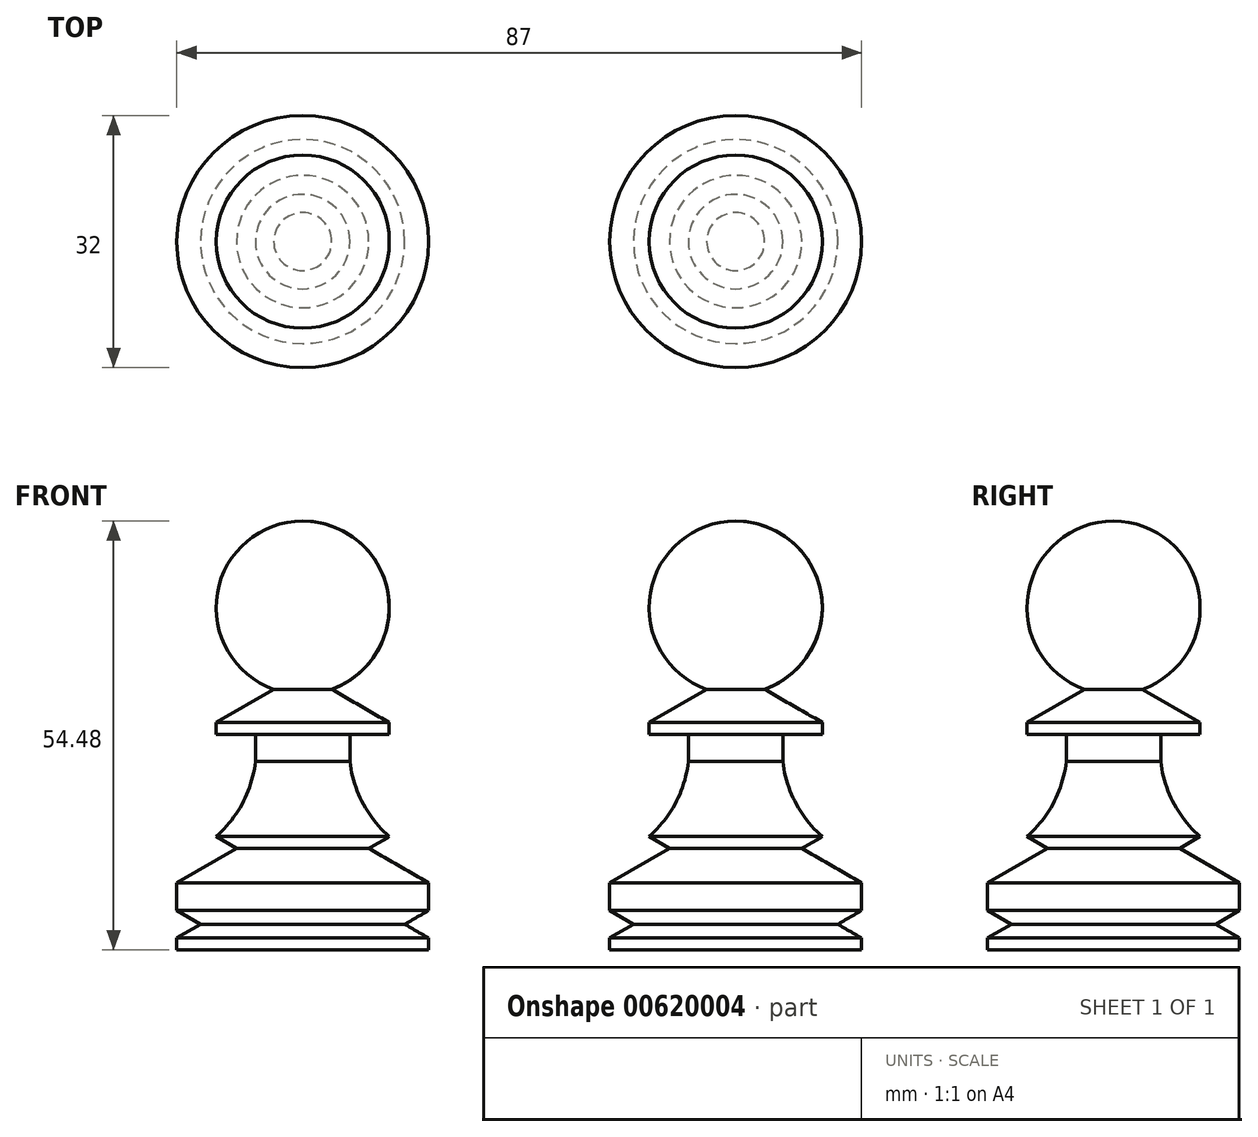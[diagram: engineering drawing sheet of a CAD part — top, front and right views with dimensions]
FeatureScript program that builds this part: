
annotation { "Feature Type Name" : "Feature", "Feature Type Description" : "" }
export const myFeature = defineFeature(function(context is Context, id is Id, definition is map)
    precondition{}
    {
        {
            var Q0;
            Q0=qCreatedBy(makeId("Front.planeOp"),FACE);
            var sketch = newSketch(context, id + "F0", { "sketchPlane" : qUnion([Q0])});
            skLineSegment(sketch, "E0", {"start": v(0, 0) * mm, "end": v(16, 0) * mm});
            skLineSegment(sketch, "E1", {"start": v(16, 0) * mm, "end": v(16, 1.5) * mm});
            skLineSegment(sketch, "E2", {"start": v(16, 1.5) * mm, "end": v(12.97, 3.25) * mm});
            skLineSegment(sketch, "E3", {"start": v(0, 0) * mm, "end": v(0, 5) * mm});
            skLineSegment(sketch, "E4", {"start": v(0, 5) * mm, "end": v(16, 5) * mm});
            skLineSegment(sketch, "E5", {"start": v(16, 5) * mm, "end": v(12.97, 3.25) * mm});
            skPoint(sketch, "E6.orphan", {"position": v(9.94, 1.5) * mm});
            skLineSegment(sketch, "E7", {"start": v(16, 5) * mm, "end": v(16, 8.5) * mm});
            skLineSegment(sketch, "E8", {"start": v(16, 8.5) * mm, "end": v(0, 8.5) * mm});
            skLineSegment(sketch, "E9", {"start": v(16, 8.5) * mm, "end": v(8.4, 12.89) * mm});
            skLineSegment(sketch, "E10", {"start": v(11, 12.89) * mm, "end": v(11, 12.89) * mm});
            skLineSegment(sketch, "E11", {"start": v(11, 56.7) * mm, "end": v(11, 27.39) * mm, "construction": true});
            skLineSegment(sketch, "E12", {"start": v(11, 14.39) * mm, "end": v(0, 14.39) * mm});
            skPoint(sketch, "E13.orphan", {"position": v(16, 13.5) * mm});
            skPoint(sketch, "E14.0.end.orphan", {"position": v(6, 13.5) * mm});
            skLineSegment(sketch, "E15", {"start": v(8.4, 12.89) * mm, "end": v(0, 12.89) * mm});
            skLineSegment(sketch, "E16", {"start": v(0, 14.39) * mm, "end": v(0, 27.39) * mm});
            skLineSegment(sketch, "E17", {"start": v(0, 27.39) * mm, "end": v(11, 27.39) * mm});
            skLineSegment(sketch, "E18", {"start": v(11, 27.39) * mm, "end": v(11, 28.89) * mm});
            skLineSegment(sketch, "E19", {"start": v(11, 28.89) * mm, "end": v(0, 28.89) * mm});
            skLineSegment(sketch, "E20", {"start": v(11, 28.89) * mm, "end": v(3.68, 33.11) * mm});
            skLineSegment(sketch, "E21", {"start": v(6, 27.39) * mm, "end": v(6, 14.39) * mm});
            skArc(sketch, "E22", {"start": v(6, 27.39) * mm, "mid": v(6.9, 20.27) * mm, "end": v(11, 14.39) * mm});
            skPoint(sketch, "E22.third.point", {"position": v(6, 23.93) * mm});
            skArc(sketch, "E23", {"start": v(3.68, 33.11) * mm, "mid": v(10.84, 45.35) * mm, "end": v(0, 54.48) * mm});
            skLineSegment(sketch, "E24", {"start": v(0, 54.48) * mm, "end": v(0, 0) * mm});
            skLineSegment(sketch, "E25", {"start": v(11, 27.39) * mm, "end": v(35.92, 27.39) * mm, "construction": true});
            skLineSegment(sketch, "E26", {"start": v(8.4, 12.89) * mm, "end": v(11, 14.39) * mm});
            skSolve(sketch);
        }
        {
            var Q0;
            Q0=qSketchRegion(id+"F0",true);
            var Q1;
            Q1=sQuery(id+"F0.wireOp",EDGE,"E24");
            revolve(context, id + "F1", {"entities" : qUnion([Q0]), "axis" : qUnion([Q1]), "revolveType" : RevolveType.FULL});
        }
        {
            var Q0;
            Q0=makeQuery(id+"F1.opRevolve","SWEPT_BODY",BODY,{"disambiguationData":[OSD([sQuery(id+"F0.wireOp",EDGE,"E0"),sQuery(id+"F0.wireOp",EDGE,"E1"),sQuery(id+"F0.wireOp",EDGE,"E2"),sQuery(id+"F0.wireOp",EDGE,"E5"),sQuery(id+"F0.wireOp",EDGE,"E7"),sQuery(id+"F0.wireOp",EDGE,"E9"),sQuery(id+"F0.wireOp",EDGE,"E17"),sQuery(id+"F0.wireOp",EDGE,"E18"),sQuery(id+"F0.wireOp",EDGE,"E20"),sQuery(id+"F0.wireOp",EDGE,"E21"),sQuery(id+"F0.wireOp",EDGE,"E22"),sQuery(id+"F0.wireOp",EDGE,"E23"),sQuery(id+"F0.wireOp",EDGE,"E24"),sQuery(id+"F0.wireOp",EDGE,"E26")])]});
            transform(context, id + "F2", {"entities" : qUnion([Q0]), "transformType" : TransformType.TRANSLATION_3D, "dx" : 0 * mm, "dy" : 0 * mm, "dz" : 0 * mm, "makeCopy" : true});
        }
        {
            var Q0;
            Q0=makeQuery(id+"F2.opPattern","COPY",BODY,{"derivedFrom":makeQuery(id+"F1.opRevolve","SWEPT_BODY",BODY,{"disambiguationData":[OSD([sQuery(id+"F0.wireOp",EDGE,"E0"),sQuery(id+"F0.wireOp",EDGE,"E1"),sQuery(id+"F0.wireOp",EDGE,"E2"),sQuery(id+"F0.wireOp",EDGE,"E5"),sQuery(id+"F0.wireOp",EDGE,"E7"),sQuery(id+"F0.wireOp",EDGE,"E9"),sQuery(id+"F0.wireOp",EDGE,"E17"),sQuery(id+"F0.wireOp",EDGE,"E18"),sQuery(id+"F0.wireOp",EDGE,"E20"),sQuery(id+"F0.wireOp",EDGE,"E21"),sQuery(id+"F0.wireOp",EDGE,"E22"),sQuery(id+"F0.wireOp",EDGE,"E23"),sQuery(id+"F0.wireOp",EDGE,"E24"),sQuery(id+"F0.wireOp",EDGE,"E26")])]}),"instanceName":"1"});
            deleteBodies(context, id + "F3", {"entities" : qUnion([Q0])});
        }
        {
            var Q0;
            Q0=makeQuery(id+"F1.opRevolve","SWEPT_BODY",BODY,{"disambiguationData":[OSD([sQuery(id+"F0.wireOp",EDGE,"E0"),sQuery(id+"F0.wireOp",EDGE,"E1"),sQuery(id+"F0.wireOp",EDGE,"E2"),sQuery(id+"F0.wireOp",EDGE,"E5"),sQuery(id+"F0.wireOp",EDGE,"E7"),sQuery(id+"F0.wireOp",EDGE,"E9"),sQuery(id+"F0.wireOp",EDGE,"E17"),sQuery(id+"F0.wireOp",EDGE,"E18"),sQuery(id+"F0.wireOp",EDGE,"E20"),sQuery(id+"F0.wireOp",EDGE,"E21"),sQuery(id+"F0.wireOp",EDGE,"E22"),sQuery(id+"F0.wireOp",EDGE,"E23"),sQuery(id+"F0.wireOp",EDGE,"E24"),sQuery(id+"F0.wireOp",EDGE,"E26")])]});
            transform(context, id + "F4", {"entities" : qUnion([Q0]), "transformType" : TransformType.TRANSLATION_3D, "dx" : 55 * mm, "dy" : 0 * mm, "dz" : 0 * mm, "makeCopy" : true});
        }
    });
